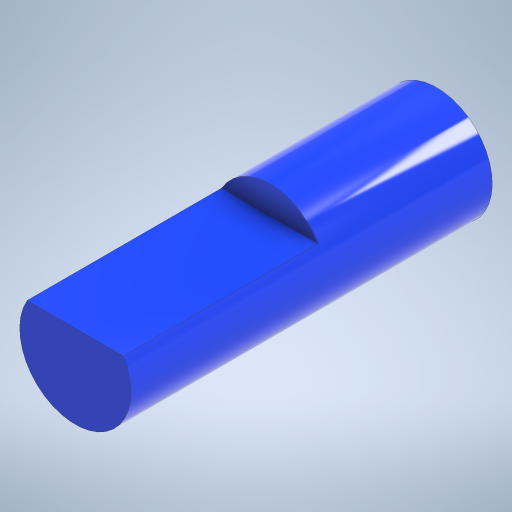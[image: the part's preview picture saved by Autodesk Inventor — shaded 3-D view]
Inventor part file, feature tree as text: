
AUTODESK INVENTOR PART (.ipt)
format: ipt  version: 2023.2 (Build 272271030, 271C)  size: 240,128 bytes
history: native  units: mm
features: extrude x2, sketch x1
ambient origin geometry x8: Origin, YZ Plane, XZ Plane, XY Plane, X Axis, Y Axis, Z Axis, Center Point
bodies: Solid1 (feature_tree)
feature tree (3):
  sketch  "Sketch1"  dims[d0=8.0mm d1=2.0mm d2=26.0mm d3=0.0mm d4=12.0mm d5=0.0mm]
  extrude  "Extrusion1"  Depth=12.0mm
  extrude  "Extrusion2"  Depth=26.0mm TaperAngle=0.0deg
